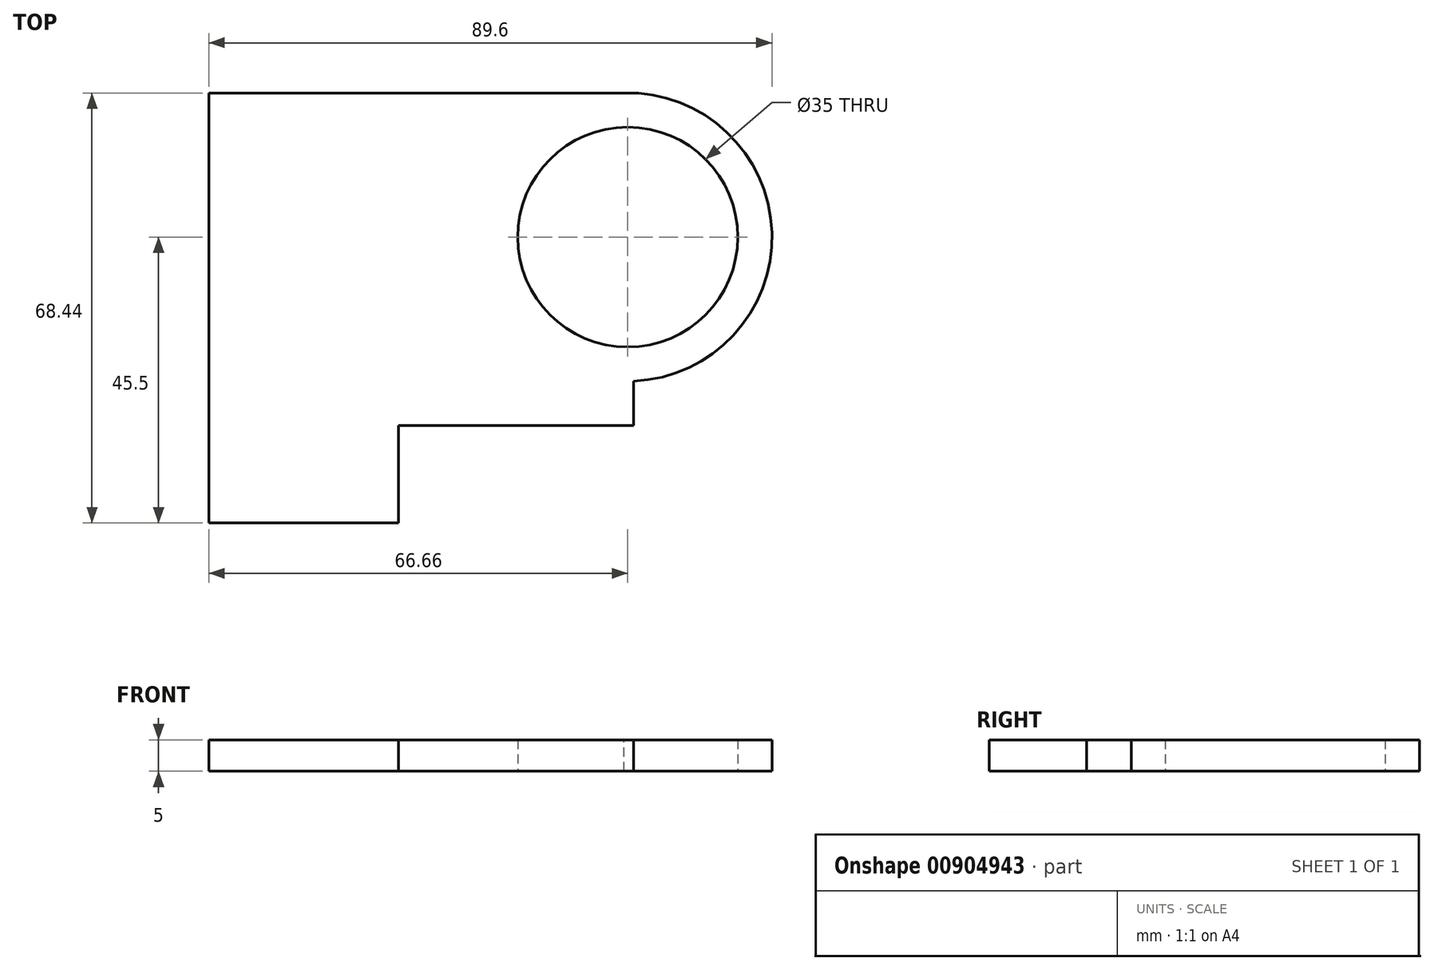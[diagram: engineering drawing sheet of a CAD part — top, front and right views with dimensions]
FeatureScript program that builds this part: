
annotation { "Feature Type Name" : "Feature", "Feature Type Description" : "" }
export const myFeature = defineFeature(function(context is Context, id is Id, definition is map)
    precondition{}
    {
        {
            var Q0;
            Q0=qCreatedBy(makeId("Top.planeOp"),FACE);
            var sketch = newSketch(context, id + "F0", { "sketchPlane" : qUnion([Q0])});
            skLineSegment(sketch, "E0.bottom", {"start": v(0, 0) * mm, "end": v(60, 0) * mm});
            skLineSegment(sketch, "E0.top", {"start": v(5, 55.23) * mm, "end": v(55, 55.23) * mm});
            skLineSegment(sketch, "E0.left", {"start": v(0, 0) * mm, "end": v(0, 50.23) * mm});
            skLineSegment(sketch, "E0.right", {"start": v(60, 0) * mm, "end": v(60, 50.23) * mm});
            skLineSegment(sketch, "E1", {"start": v(30, 0) * mm, "end": v(30, 55.23) * mm, "construction": true});
            skCircle(sketch, "E2", {"center": v(30, 30) * mm, "radius": 17.5 * mm});
            skPoint(sketch, "E3.visualSharp", {"position": v(0, 55.23) * mm});
            skArc(sketch, "E3.filletArc", {"start": v(5, 55.23) * mm, "mid": v(1.46, 53.77) * mm, "end": v(0, 50.23) * mm});
            skPoint(sketch, "E4.visualSharp", {"position": v(60, 55.23) * mm});
            skArc(sketch, "E4.filletArc", {"start": v(60, 50.23) * mm, "mid": v(58.54, 53.77) * mm, "end": v(55, 55.23) * mm});
            skSolve(sketch);
        }
        {
            var Q0;
            Q0=qSketchRegion(id+"F0",true);
            extrude(context, id + "F1", {"entities" : qUnion([Q0]), "depth" : 5 * mm, "offsetDistance" : 25 * mm});
        }
        {
            var Q0;
            Q0=makeQuery(id+"F1.opExtrude","CAP_FACE",FACE,{"disambiguationData":[OSD([sQuery(id+"F0.wireOp",EDGE,"E0.bottom"),sQuery(id+"F0.wireOp",EDGE,"E0.top"),sQuery(id+"F0.wireOp",EDGE,"E0.left"),sQuery(id+"F0.wireOp",EDGE,"E0.right"),sQuery(id+"F0.wireOp",EDGE,"E2"),sQuery(id+"F0.wireOp",EDGE,"E3.filletArc"),sQuery(id+"F0.wireOp",EDGE,"E4.filletArc")])],"isStart":false});
            var sketch = newSketch(context, id + "F2", { "sketchPlane" : qUnion([Q0])});
            skLineSegment(sketch, "E5", {"start": v(0, 36.83) * mm, "end": v(-6.45, 36.83) * mm});
            skLineSegment(sketch, "E6", {"start": v(-6.45, 36.83) * mm, "end": v(-6.45, -38.62) * mm});
            skLineSegment(sketch, "E7", {"start": v(-6.45, -38.62) * mm, "end": v(0, -38.62) * mm});
            skLineSegment(sketch, "E8", {"start": v(0, -38.62) * mm, "end": v(0, 0) * mm});
            skLineSegment(sketch, "E9", {"start": v(-6.45, -38.62) * mm, "end": v(-36.66, -38.62) * mm});
            skLineSegment(sketch, "E10", {"start": v(-36.66, -38.62) * mm, "end": v(-36.66, 55.23) * mm});
            skLineSegment(sketch, "E11", {"start": v(-36.66, 55.23) * mm, "end": v(5.84, 55.23) * mm});
            skLineSegment(sketch, "E12", {"start": v(0, 0) * mm, "end": v(-6.45, 0) * mm});
            skSolve(sketch);
        }
        {
            var Q0;
            {var subQ1=sQuery(id+"F2.wireOp",EDGE,"E5");Q0=makeQuery(id+"F2.imprint","IMPRINT",FACE,{"disambiguationData":[TD([[makeQuery(id+"F2.imprint","IMPRINT",EDGE,{"derivedFrom":subQ1}),1.0]])]});}
            var Q1;
            {var subQ4=sQuery(id+"F2.wireOp",EDGE,"E5");Q1=makeQuery(id+"F2.imprint","IMPRINT",FACE,{"disambiguationData":[TD([[makeQuery(id+"F2.imprint","IMPRINT",EDGE,{"derivedFrom":subQ4}),-1.0]])]});}
            extrude(context, id + "F3", {"entities" : qUnion([Q0, Q1]), "operationType" : NewBodyOperationType.ADD, "oppositeDirection" : true, "depth" : 5 * mm, "offsetDistance" : 25 * mm});
        }
        {
            var Q0;
            {var subQ0=sQuery(id+"F0.wireOp",EDGE,"E0.left");Q0=makeQuery(id+"F3.boolean.opBoolean","MERGE",FACE,{"derivedFrom":[makeQuery(id+"F1.opExtrude","CAP_FACE",FACE,{"disambiguationData":[OSD([sQuery(id+"F0.wireOp",EDGE,"E0.bottom"),sQuery(id+"F0.wireOp",EDGE,"E0.top"),subQ0,sQuery(id+"F0.wireOp",EDGE,"E0.right"),sQuery(id+"F0.wireOp",EDGE,"E2"),sQuery(id+"F0.wireOp",EDGE,"E3.filletArc"),sQuery(id+"F0.wireOp",EDGE,"E4.filletArc")])],"isStart":false}),makeQuery(id+"F3.opExtrude","CAP_FACE",FACE,{"disambiguationData":[OSD([subQ0,sQuery(id+"F2.wireOp",EDGE,"E5"),sQuery(id+"F2.wireOp",EDGE,"E6"),sQuery(id+"F2.wireOp",EDGE,"E7"),sQuery(id+"F2.wireOp",EDGE,"E8")])],"isStart":true})]});}
            var sketch = newSketch(context, id + "F4", { "sketchPlane" : qUnion([Q0])});
            skLineSegment(sketch, "E13", {"start": v(49.35, 0) * mm, "end": v(66.44, 0) * mm});
            skLineSegment(sketch, "E14", {"start": v(66.44, 0) * mm, "end": v(66.44, 55.23) * mm});
            skLineSegment(sketch, "E15", {"start": v(66.44, 55.23) * mm, "end": v(49.35, 55.23) * mm});
            skLineSegment(sketch, "E16", {"start": v(54.2, 0) * mm, "end": v(54.2, 55.23) * mm});
            skLineSegment(sketch, "E17", {"start": v(54.2, 55.23) * mm, "end": v(49.35, 55.23) * mm});
            skSolve(sketch);
        }
        {
            var Q0;
            Q0=qSketchRegion(id+"F4",true);
            extrude(context, id + "F5", {"entities" : qUnion([Q0]), "operationType" : NewBodyOperationType.REMOVE, "oppositeDirection" : true, "depth" : 25 * mm, "offsetDistance" : 25 * mm});
        }
        {
            var Q0;
            {var subQ0=sQuery(id+"F0.wireOp",EDGE,"E3.filletArc");var subQ1=sQuery(id+"F0.wireOp",EDGE,"E0.left");Q0=makeQuery(id+"F3.boolean.opBoolean","MERGE",FACE,{"derivedFrom":[makeQuery(id+"F1.opExtrude","CAP_FACE",FACE,{"disambiguationData":[OSD([sQuery(id+"F0.wireOp",EDGE,"E0.bottom"),sQuery(id+"F0.wireOp",EDGE,"E0.top"),subQ1,sQuery(id+"F0.wireOp",EDGE,"E0.right"),sQuery(id+"F0.wireOp",EDGE,"E2"),subQ0,sQuery(id+"F0.wireOp",EDGE,"E4.filletArc")])],"isStart":false}),makeQuery(id+"F3.opExtrude","CAP_FACE",FACE,{"disambiguationData":[OSD([subQ1,subQ0,sQuery(id+"F2.wireOp",EDGE,"E6"),sQuery(id+"F2.wireOp",EDGE,"E9"),sQuery(id+"F2.wireOp",EDGE,"E10"),sQuery(id+"F2.wireOp",EDGE,"E11"),sQuery(id+"F2.wireOp",EDGE,"E12")])],"isStart":true})]});}
            var sketch = newSketch(context, id + "F6", { "sketchPlane" : qUnion([Q0])});
            skCircle(sketch, "E18", {"center": v(30, 30) * mm, "radius": 22.94 * mm});
            skLineSegment(sketch, "E19", {"start": v(29.4, 52.94) * mm, "end": v(-36.66, 52.94) * mm});
            skLineSegment(sketch, "E20", {"start": v(30.91, 7.07) * mm, "end": v(30.91, 0) * mm});
            skLineSegment(sketch, "E21", {"start": v(30.91, 0) * mm, "end": v(-36.66, 0) * mm});
            skLineSegment(sketch, "E22", {"start": v(-36.66, 0) * mm, "end": v(-36.66, 52.94) * mm});
            skSolve(sketch);
        }
        {
            var Q0;
            {var subQ4=sQuery(id+"F6.wireOp",EDGE,"E19");Q0=makeQuery(id+"F6.imprint","IMPRINT",FACE,{"disambiguationData":[TD([[makeQuery(id+"F6.imprint","IMPRINT",EDGE,{"derivedFrom":subQ4}),-1.0]])]});}
            extrude(context, id + "F7", {"entities" : qUnion([Q0]), "operationType" : NewBodyOperationType.REMOVE, "oppositeDirection" : true, "depth" : 25 * mm, "offsetDistance" : 25 * mm});
        }
        {
            var Q0;
            {var subQ0=sQuery(id+"F0.wireOp",EDGE,"E3.filletArc");var subQ1=sQuery(id+"F0.wireOp",EDGE,"E0.left");Q0=makeQuery(id+"F3.boolean.opBoolean","MERGE",FACE,{"derivedFrom":[makeQuery(id+"F1.opExtrude","CAP_FACE",FACE,{"disambiguationData":[OSD([sQuery(id+"F0.wireOp",EDGE,"E0.bottom"),sQuery(id+"F0.wireOp",EDGE,"E0.top"),subQ1,sQuery(id+"F0.wireOp",EDGE,"E0.right"),sQuery(id+"F0.wireOp",EDGE,"E2"),subQ0,sQuery(id+"F0.wireOp",EDGE,"E4.filletArc")])],"isStart":false}),makeQuery(id+"F3.opExtrude","CAP_FACE",FACE,{"disambiguationData":[OSD([subQ1,subQ0,sQuery(id+"F2.wireOp",EDGE,"E6"),sQuery(id+"F2.wireOp",EDGE,"E9"),sQuery(id+"F2.wireOp",EDGE,"E10"),sQuery(id+"F2.wireOp",EDGE,"E11"),sQuery(id+"F2.wireOp",EDGE,"E12")])],"isStart":true})]});}
            var sketch = newSketch(context, id + "F8", { "sketchPlane" : qUnion([Q0])});
            skLineSegment(sketch, "E23", {"start": v(-6.45, 0) * mm, "end": v(-6.45, -15.5) * mm});
            skLineSegment(sketch, "E24", {"start": v(-6.45, -15.5) * mm, "end": v(-36.66, -15.5) * mm});
            skLineSegment(sketch, "E25", {"start": v(-36.66, -15.5) * mm, "end": v(-36.66, -38.62) * mm});
            skLineSegment(sketch, "E26", {"start": v(-36.66, -38.62) * mm, "end": v(-6.45, -38.62) * mm});
            skLineSegment(sketch, "E27", {"start": v(-6.45, -38.62) * mm, "end": v(-6.45, -15.5) * mm});
            skSolve(sketch);
        }
        {
            var Q0;
            Q0=qSketchRegion(id+"F8",true);
            extrude(context, id + "F9", {"entities" : qUnion([Q0]), "operationType" : NewBodyOperationType.REMOVE, "oppositeDirection" : true, "depth" : 25 * mm, "offsetDistance" : 25 * mm});
        }
    });
